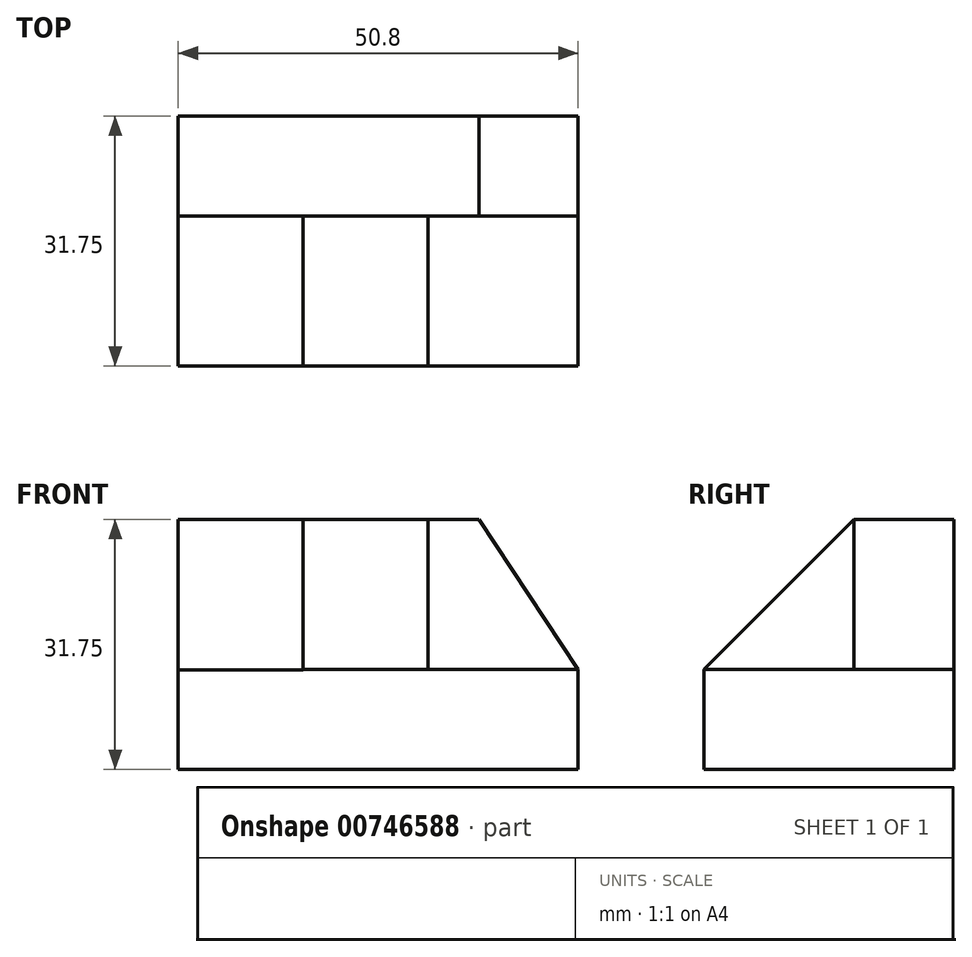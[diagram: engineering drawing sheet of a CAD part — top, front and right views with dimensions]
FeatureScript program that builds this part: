
annotation { "Feature Type Name" : "Feature", "Feature Type Description" : "" }
export const myFeature = defineFeature(function(context is Context, id is Id, definition is map)
    precondition{}
    {
        {
            var Q0;
            Q0=qCreatedBy(makeId("Front.planeOp"),FACE);
            var sketch = newSketch(context, id + "F0", { "sketchPlane" : qUnion([Q0])});
            skLineSegment(sketch, "E0", {"start": v(0, 0) * mm, "end": v(0, 31.75) * mm});
            skLineSegment(sketch, "E1", {"start": v(0, 31.75) * mm, "end": v(50.8, 31.75) * mm});
            skLineSegment(sketch, "E2", {"start": v(50.8, 31.75) * mm, "end": v(50.8, 0) * mm});
            skLineSegment(sketch, "E3", {"start": v(50.8, 0) * mm, "end": v(0, 0) * mm});
            skSolve(sketch);
        }
        {
            var Q0;
            Q0=makeQuery(id+"F0.imprint","IMPRINT",FACE,{"disambiguationData":[TD([[makeQuery(id+"F0.imprint","IMPRINT",EDGE,{"derivedFrom":sQuery(id+"F0.wireOp",EDGE,"E0")}),-1.0]])]});
            extrude(context, id + "F1", {"entities" : qUnion([Q0]), "depth" : 31.75 * mm, "offsetDistance" : 25.4 * mm});
        }
        {
            var Q0;
            Q0=makeQuery(id+"F1.opExtrude","CAP_FACE",FACE,{"disambiguationData":[OSD([sQuery(id+"F0.wireOp",EDGE,"E0"),sQuery(id+"F0.wireOp",EDGE,"E1"),sQuery(id+"F0.wireOp",EDGE,"E2"),sQuery(id+"F0.wireOp",EDGE,"E3")])],"isStart":false});
            var sketch = newSketch(context, id + "F2", { "sketchPlane" : qUnion([Q0])});
            skLineSegment(sketch, "E4", {"start": v(31.75, 31.75) * mm, "end": v(31.75, 12.7) * mm});
            skLineSegment(sketch, "E5", {"start": v(31.75, 12.7) * mm, "end": v(50.8, 12.7) * mm});
            skLineSegment(sketch, "E6", {"start": v(50.8, 12.7) * mm, "end": v(50.8, 31.75) * mm});
            skLineSegment(sketch, "E7", {"start": v(50.8, 31.75) * mm, "end": v(31.75, 31.75) * mm});
            skSolve(sketch);
        }
        {
            var Q0;
            Q0=makeQuery(id+"F2.imprint","IMPRINT",FACE,{"disambiguationData":[TD([[makeQuery(id+"F2.imprint","IMPRINT",EDGE,{"derivedFrom":sQuery(id+"F2.wireOp",EDGE,"E4")}),1.0]])]});
            extrude(context, id + "F3", {"entities" : qUnion([Q0]), "operationType" : NewBodyOperationType.REMOVE, "oppositeDirection" : true, "depth" : 19.05 * mm, "offsetDistance" : 25.4 * mm});
        }
        {
            var Q0;
            Q0=makeQuery(id+"F3.boolean.opBoolean","COPY",FACE,{"derivedFrom":makeQuery(id+"F3.opExtrude","CAP_FACE",FACE,{"disambiguationData":[OSD([sQuery(id+"F2.wireOp",EDGE,"E4"),sQuery(id+"F2.wireOp",EDGE,"E5"),sQuery(id+"F2.wireOp",EDGE,"E6"),sQuery(id+"F2.wireOp",EDGE,"E7")])],"isStart":false})});
            var sketch = newSketch(context, id + "F4", { "sketchPlane" : qUnion([Q0])});
            skLineSegment(sketch, "E8", {"start": v(38.1, 31.93) * mm, "end": v(50.8, 12.7) * mm});
            skLineSegment(sketch, "E9", {"start": v(38.1, 31.93) * mm, "end": v(50.8, 31.75) * mm});
            skLineSegment(sketch, "E10", {"start": v(50.8, 31.75) * mm, "end": v(50.8, 12.7) * mm});
            skSolve(sketch);
        }
        {
            var Q0;
            {var subQ0=sQuery(id+"F4.wireOp",EDGE,"E10");Q0=makeQuery(id+"F4.imprint","IMPRINT",FACE,{"disambiguationData":[TD([[makeQuery(id+"F4.imprint","IMPRINT",EDGE,{"derivedFrom":subQ0}),-1.0]])]});}
            extrude(context, id + "F5", {"entities" : qUnion([Q0]), "operationType" : NewBodyOperationType.REMOVE, "oppositeDirection" : true, "depth" : 25.4 * mm, "offsetDistance" : 25.4 * mm});
        }
        {
            var Q0;
            Q0=makeQuery(id+"F1.opExtrude","CAP_FACE",FACE,{"disambiguationData":[OSD([sQuery(id+"F0.wireOp",EDGE,"E0"),sQuery(id+"F0.wireOp",EDGE,"E1"),sQuery(id+"F0.wireOp",EDGE,"E2"),sQuery(id+"F0.wireOp",EDGE,"E3")])],"isStart":false});
            var sketch = newSketch(context, id + "F6", { "sketchPlane" : qUnion([Q0])});
            skLineSegment(sketch, "E11", {"start": v(15.88, 31.75) * mm, "end": v(15.88, 12.63) * mm});
            skLineSegment(sketch, "E12", {"start": v(15.88, 12.63) * mm, "end": v(0, 12.63) * mm});
            skLineSegment(sketch, "E13", {"start": v(0, 12.63) * mm, "end": v(0, 31.75) * mm});
            skLineSegment(sketch, "E14", {"start": v(0, 31.75) * mm, "end": v(15.88, 31.75) * mm});
            skSolve(sketch);
        }
        {
            var Q0;
            Q0=makeQuery(id+"F6.imprint","IMPRINT",FACE,{"disambiguationData":[TD([[makeQuery(id+"F6.imprint","IMPRINT",EDGE,{"derivedFrom":sQuery(id+"F6.wireOp",EDGE,"E11")}),-1.0]])]});
            extrude(context, id + "F7", {"entities" : qUnion([Q0]), "operationType" : NewBodyOperationType.REMOVE, "oppositeDirection" : true, "depth" : 19.05 * mm, "offsetDistance" : 25.4 * mm});
        }
        {
            var Q0;
            Q0=makeQuery(id+"F3.boolean.opBoolean","COPY",FACE,{"derivedFrom":makeQuery(id+"F3.opExtrude","SWEPT_FACE",FACE,{"disambiguationData":[OSD([sQuery(id+"F2.wireOp",EDGE,"E4")])]})});
            var sketch = newSketch(context, id + "F8", { "sketchPlane" : qUnion([Q0])});
            skLineSegment(sketch, "E15", {"start": v(-12.7, 31.75) * mm, "end": v(-31.75, 12.7) * mm});
            skLineSegment(sketch, "E16", {"start": v(-31.75, 12.7) * mm, "end": v(-31.75, 31.75) * mm});
            skLineSegment(sketch, "E17", {"start": v(-31.75, 31.75) * mm, "end": v(-12.7, 31.75) * mm});
            skSolve(sketch);
        }
        {
            var Q0;
            Q0=makeQuery(id+"F8.imprint","IMPRINT",FACE,{"disambiguationData":[TD([[makeQuery(id+"F8.imprint","IMPRINT",EDGE,{"derivedFrom":sQuery(id+"F8.wireOp",EDGE,"E15")}),-1.0]])]});
            extrude(context, id + "F9", {"entities" : qUnion([Q0]), "operationType" : NewBodyOperationType.REMOVE, "oppositeDirection" : true, "depth" : 25.4 * mm, "offsetDistance" : 25.4 * mm});
        }
    });
